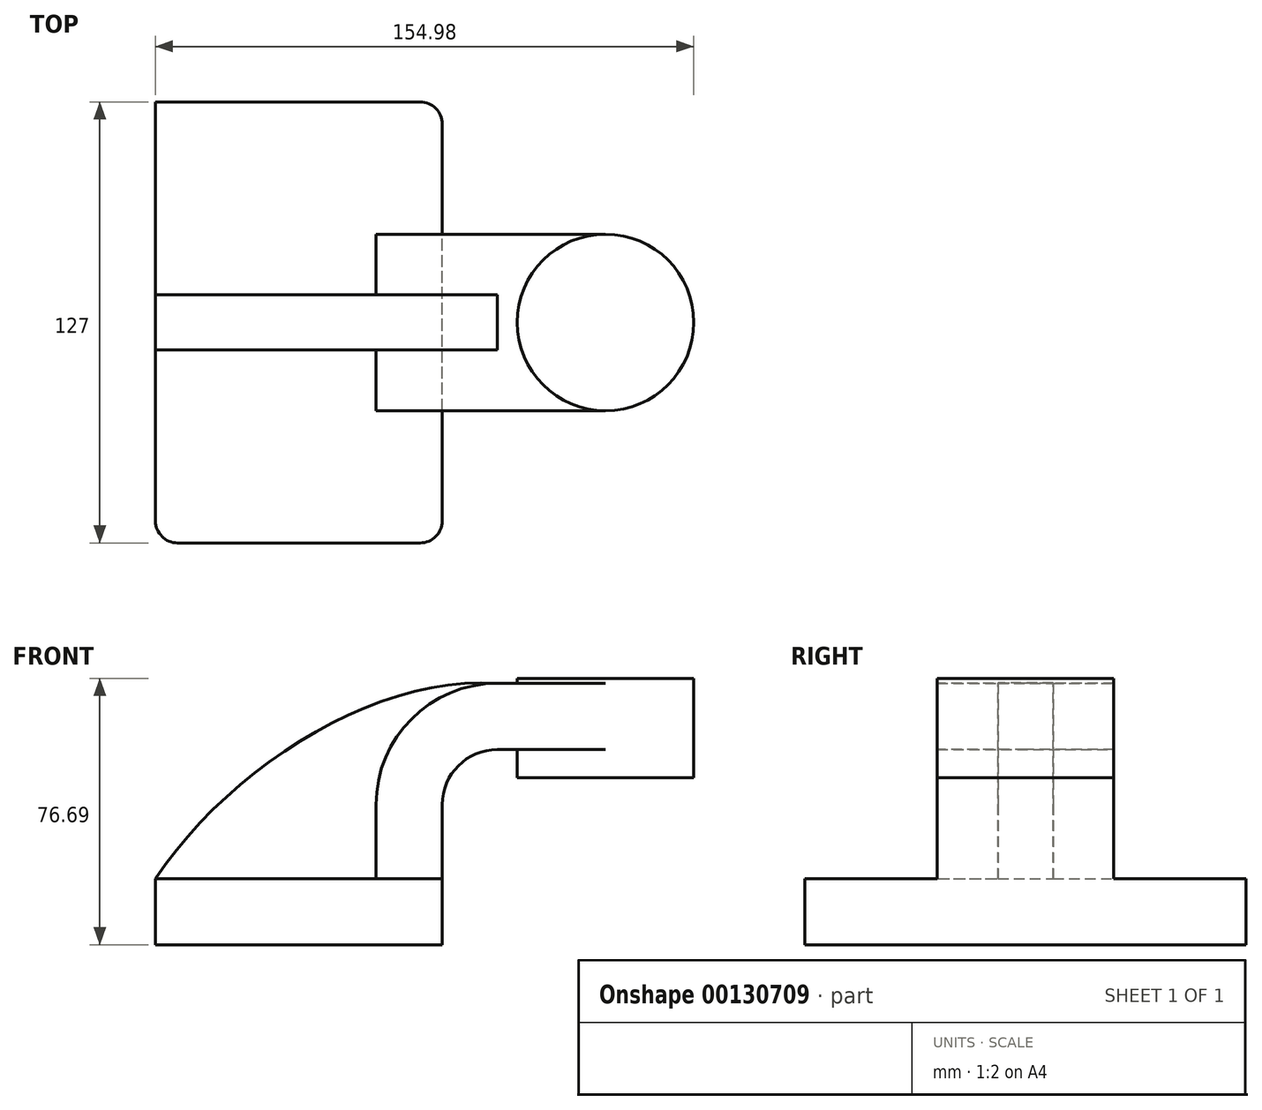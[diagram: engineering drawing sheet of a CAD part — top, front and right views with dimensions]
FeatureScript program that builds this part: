
annotation { "Feature Type Name" : "Feature", "Feature Type Description" : "" }
export const myFeature = defineFeature(function(context is Context, id is Id, definition is map)
    precondition{}
    {
        {
            var Q0;
            Q0=qCreatedBy(makeId("Front.planeOp"),FACE);
            var sketch = newSketch(context, id + "F0", { "sketchPlane" : qUnion([Q0])});
            skLineSegment(sketch, "E0.bottom", {"start": v(-41.28, -9.53) * mm, "end": v(41.28, -9.53) * mm});
            skLineSegment(sketch, "E0.top", {"start": v(-41.28, 9.53) * mm, "end": v(41.28, 9.53) * mm});
            skLineSegment(sketch, "E0.left", {"start": v(-41.28, -9.53) * mm, "end": v(-41.28, 9.53) * mm});
            skLineSegment(sketch, "E0.right", {"start": v(41.28, -9.53) * mm, "end": v(41.28, 9.53) * mm});
            skPoint(sketch, "E0.middle", {"position": v(0, 0) * mm});
            skLineSegment(sketch, "E1.bottom", {"start": v(62.9, 67.16) * mm, "end": v(113.7, 67.16) * mm});
            skLineSegment(sketch, "E1.top", {"start": v(62.9, 38.58) * mm, "end": v(113.7, 38.58) * mm});
            skLineSegment(sketch, "E1.left", {"start": v(62.9, 67.16) * mm, "end": v(62.9, 38.58) * mm});
            skLineSegment(sketch, "E1.right", {"start": v(113.7, 67.16) * mm, "end": v(113.7, 38.58) * mm});
            skPoint(sketch, "E1.middle", {"position": v(88.3, 52.87) * mm});
            skLineSegment(sketch, "E2", {"start": v(41.28, 30.8) * mm, "end": v(41.28, 9.53) * mm});
            skArc(sketch, "E3", {"start": v(41.28, 30.8) * mm, "mid": v(45.92, 42.03) * mm, "end": v(57.15, 46.68) * mm});
            skLineSegment(sketch, "E4", {"start": v(57.15, 46.68) * mm, "end": v(88.3, 46.68) * mm});
            skLineSegment(sketch, "E5.0", {"start": v(22.23, 30.8) * mm, "end": v(22.23, 9.52) * mm});
            skArc(sketch, "E5.1", {"start": v(22.23, 30.8) * mm, "mid": v(32.45, 55.5) * mm, "end": v(57.15, 65.73) * mm});
            skLineSegment(sketch, "E5.2", {"start": v(57.15, 65.73) * mm, "end": v(88.3, 65.73) * mm});
            skLineSegment(sketch, "E6", {"start": v(88.3, 38.58) * mm, "end": v(88.3, 67.16) * mm});
            skFitSpline(sketch, "E7", {"points": [v(-41.28, 9.53) * mm, v(57.15, 65.73) * mm], "startDerivative": vector(64.21, 95.83) * mm, "endDerivative": vector(106.9, -7.05) * mm});
            skSolve(sketch);
        }
        {
            var Q0;
            Q0=makeQuery(id+"F0.imprint","IMPRINT",FACE,{"disambiguationData":[TD([[makeQuery(id+"F0.imprint","IMPRINT",EDGE,{"derivedFrom":sQuery(id+"F0.wireOp",EDGE,"E0.bottom")}),1.0]])]});
            extrude(context, id + "F1", {"entities" : qUnion([Q0]), "endBound" : BoundingType.SYMMETRIC, "depth" : 127 * mm});
        }
        {
            var Q0;
            {var subQ2=sQuery(id+"F0.wireOp",EDGE,"E2");Q0=makeQuery(id+"F0.imprint","IMPRINT",FACE,{"disambiguationData":[TD([[makeQuery(id+"F0.imprint","IMPRINT",EDGE,{"derivedFrom":subQ2}),-1.0]])]});}
            var Q1;
            {var subQ0=sQuery(id+"F0.wireOp",EDGE,"E5.2");var subQ1=sQuery(id+"F0.wireOp",EDGE,"E1.left");var subQ2=makeQuery(id+"F0.imprint","INTERSECT",VERTEX,{"derivedFrom":[subQ1,subQ0]});Q1=makeQuery(id+"F0.imprint","IMPRINT",FACE,{"disambiguationData":[TD([[makeQuery(id+"F0.imprint","IMPRINT",EDGE,{"disambiguationData":[TD([[subQ2,-1.0]])],"derivedFrom":subQ1}),1.0]])]});}
            extrude(context, id + "F2", {"entities" : qUnion([Q0, Q1]), "operationType" : NewBodyOperationType.ADD, "endBound" : BoundingType.SYMMETRIC, "depth" : 50.8 * mm});
        }
        {
            var Q0;
            {var subQ2=sQuery(id+"F0.wireOp",EDGE,"E5.0");Q0=makeQuery(id+"F0.imprint","IMPRINT",FACE,{"disambiguationData":[TD([[makeQuery(id+"F0.imprint","IMPRINT",EDGE,{"derivedFrom":subQ2}),-1.0]])]});}
            extrude(context, id + "F3", {"entities" : qUnion([Q0]), "operationType" : NewBodyOperationType.ADD, "endBound" : BoundingType.SYMMETRIC, "depth" : 15.88 * mm});
        }
        {
            var Q0;
            {var subQ0=sQuery(id+"F0.wireOp",EDGE,"E1.right");Q0=makeQuery(id+"F0.imprint","IMPRINT",FACE,{"disambiguationData":[TD([[makeQuery(id+"F0.imprint","IMPRINT",EDGE,{"derivedFrom":subQ0}),-1.0]])]});}
            var Q1;
            Q1=sQuery(id+"F0.wireOp",EDGE,"E6");
            revolve(context, id + "F4", {"operationType" : NewBodyOperationType.ADD, "entities" : qUnion([Q0]), "axis" : qUnion([Q1]), "revolveType" : RevolveType.FULL});
        }
        {
            var Q0;
            Q0=makeQuery(id+"F1.opExtrude","CAP_EDGE",EDGE,{"disambiguationData":[OSD([sQuery(id+"F0.wireOp",EDGE,"E0.right")])],"isStart":false});
            var Q1;
            Q1=makeQuery(id+"F1.opExtrude","CAP_EDGE",EDGE,{"disambiguationData":[OSD([sQuery(id+"F0.wireOp",EDGE,"E0.left")])],"isStart":false});
            var Q2;
            Q2=makeQuery(id+"F1.opExtrude","CAP_EDGE",EDGE,{"disambiguationData":[OSD([sQuery(id+"F0.wireOp",EDGE,"E0.right")])],"isStart":true});
            fillet(context, id + "F5", {"entities" : qUnion([Q0, Q1, Q2]), "radius" : 6.35 * mm, "tangentPropagation" : true, "allowEdgeOverflow" : false});
        }
    });
